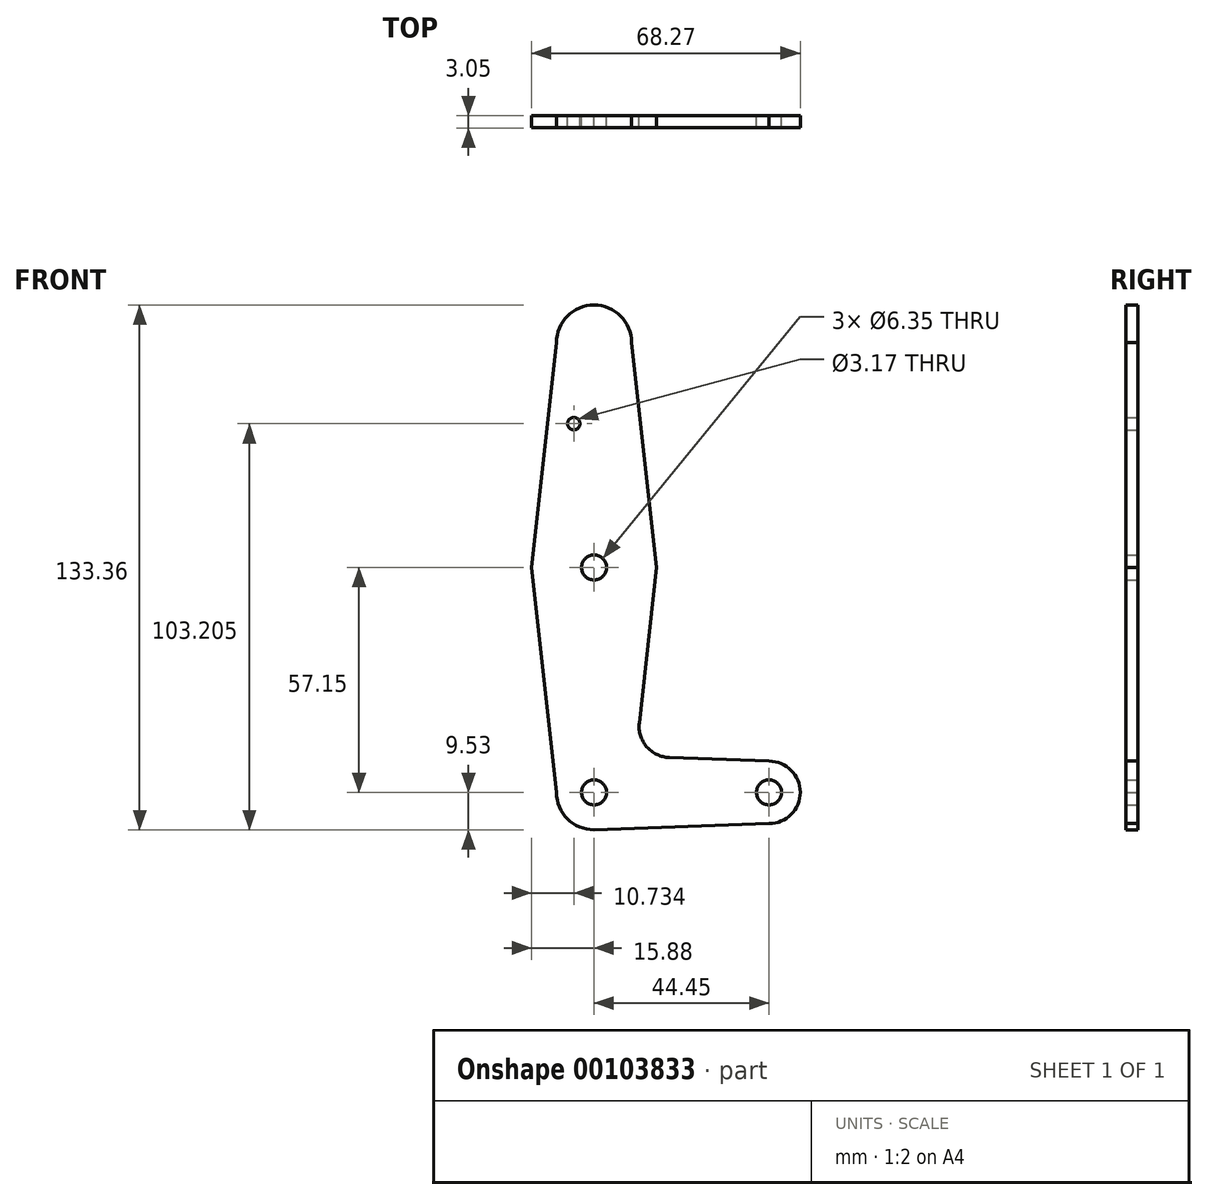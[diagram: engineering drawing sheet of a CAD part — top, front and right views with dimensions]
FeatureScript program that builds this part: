
annotation { "Feature Type Name" : "Feature", "Feature Type Description" : "" }
export const myFeature = defineFeature(function(context is Context, id is Id, definition is map)
    precondition{}
    {
        {
            var Q0;
            Q0=qCreatedBy(makeId("Front.planeOp"),FACE);
            var sketch = newSketch(context, id + "F0", { "sketchPlane" : qUnion([Q0])});
            skLineSegment(sketch, "E0", {"start": v(0, 0) * mm, "end": v(0, 114.3) * mm, "construction": true});
            skLineSegment(sketch, "E1", {"start": v(0, 0) * mm, "end": v(44.45, 0) * mm, "construction": true});
            skCircle(sketch, "E2", {"center": v(0, 114.3) * mm, "radius": 9.53 * mm});
            skCircle(sketch, "E3", {"center": v(0, 57.15) * mm, "radius": 15.88 * mm});
            skCircle(sketch, "E4", {"center": v(0, 0) * mm, "radius": 9.53 * mm});
            skCircle(sketch, "E5", {"center": v(44.45, 0) * mm, "radius": 7.94 * mm});
            skLineSegment(sketch, "E6", {"start": v(-9.53, 114.3) * mm, "end": v(-15.88, 57.15) * mm});
            skLineSegment(sketch, "E7", {"start": v(-15.88, 57.15) * mm, "end": v(-9.52, 0) * mm});
            skLineSegment(sketch, "E8", {"start": v(9.52, 114.3) * mm, "end": v(15.88, 57.15) * mm});
            skLineSegment(sketch, "E9", {"start": v(15.88, 57.15) * mm, "end": v(11.49, 17.67) * mm});
            skLineSegment(sketch, "E10", {"start": v(19.1, 8.84) * mm, "end": v(44.45, 7.94) * mm});
            skLineSegment(sketch, "E11", {"start": v(0, -9.52) * mm, "end": v(44.45, -7.94) * mm});
            skCircle(sketch, "E12", {"center": v(0, 114.3) * mm, "radius": 3.18 * mm});
            skCircle(sketch, "E13", {"center": v(0, 57.15) * mm, "radius": 3.18 * mm});
            skCircle(sketch, "E14", {"center": v(0, 0) * mm, "radius": 3.18 * mm});
            skCircle(sketch, "E15", {"center": v(44.45, 0) * mm, "radius": 3.18 * mm});
            skArc(sketch, "E16.filletArc", {"start": v(11.49, 17.67) * mm, "mid": v(13.37, 11.6) * mm, "end": v(19.1, 8.84) * mm});
            skCircle(sketch, "E17", {"center": v(-5.15, 93.68) * mm, "radius": 1.59 * mm});
            skSolve(sketch);
        }
        {
            var Q0;
            Q0=makeQuery(id+"F0.imprint","IMPRINT",FACE,{"disambiguationData":[TD([[makeQuery(id+"F0.imprint","IMPRINT",EDGE,{"derivedFrom":sQuery(id+"F0.wireOp",EDGE,"E12")}),-1.0]])]});
            var Q1;
            Q1=makeQuery(id+"F0.imprint","IMPRINT",FACE,{"disambiguationData":[TD([[makeQuery(id+"F0.imprint","IMPRINT",EDGE,{"derivedFrom":sQuery(id+"F0.wireOp",EDGE,"E12")}),1.0]])]});
            var Q2;
            Q2=makeQuery(id+"F0.imprint","IMPRINT",FACE,{"disambiguationData":[TD([[makeQuery(id+"F0.imprint","IMPRINT",EDGE,{"derivedFrom":sQuery(id+"F0.wireOp",EDGE,"E17")}),-1.0]])]});
            var Q3;
            Q3=makeQuery(id+"F0.imprint","IMPRINT",FACE,{"disambiguationData":[TD([[makeQuery(id+"F0.imprint","IMPRINT",EDGE,{"derivedFrom":sQuery(id+"F0.wireOp",EDGE,"E13")}),-1.0]])]});
            var Q4;
            {var subQ5=sQuery(id+"F0.wireOp",EDGE,"E10");Q4=makeQuery(id+"F0.imprint","IMPRINT",FACE,{"disambiguationData":[TD([[makeQuery(id+"F0.imprint","IMPRINT",EDGE,{"derivedFrom":subQ5}),-1.0]])]});}
            var Q5;
            Q5=makeQuery(id+"F0.imprint","IMPRINT",FACE,{"disambiguationData":[TD([[makeQuery(id+"F0.imprint","IMPRINT",EDGE,{"derivedFrom":sQuery(id+"F0.wireOp",EDGE,"E14")}),-1.0]])]});
            var Q6;
            Q6=makeQuery(id+"F0.imprint","IMPRINT",FACE,{"disambiguationData":[TD([[makeQuery(id+"F0.imprint","IMPRINT",EDGE,{"derivedFrom":sQuery(id+"F0.wireOp",EDGE,"E15")}),-1.0]])]});
            extrude(context, id + "F1", {"entities" : qUnion([Q0, Q1, Q2, Q3, Q4, Q5, Q6]), "depth" : 3.05 * mm});
        }
    });
